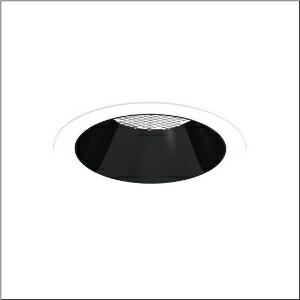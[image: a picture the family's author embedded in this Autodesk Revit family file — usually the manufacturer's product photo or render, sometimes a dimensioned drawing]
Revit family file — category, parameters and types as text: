
# Revit family: lunis_21_xl_51db17ef91c
name_source: partatom
category: Lighting Fixtures
units: mm (PartAtom-declared; Revit-internal decimal feet)

## family parameters
Cut with Voids When Loaded = No
Host = Face
Light Source = No
Part Type = Normal
Room Calculation Point = No
Round Connector Dimension = Use Diameter
Shared = No

## types (1)
- --- (1 x LED, 3480 lm, 25.4 W, 6500K)
    Apparent Load = 25 VA
    CIE Flux Codes = 92 100 100 100 100
    Color Rendering = 80
    Color Temperature = 6500K
    Default Elevation = 1800 mm
    Description = Lunis 21,  XL, downlight, light control with lens, of PMMA, anti glare with reflector, of PC, light emission: direct distribution, LED rated luminous flux: 2.060lm, light colour: 830/840/865, with terminal, 5-pole, mains connection: 220..240V, AC/DC, 0/50..60Hz, housing, round, of diecast aluminium, traffic white (RAL 9016), diameter: 230mm, clamping range: 1..40mm, protection rating (complete): IP20, protection rating (on room side): IP54, insulation class (complete): insulation class II (safety insulation), certification: CE, impact resistance: IK03, packaging unit: 1 piece
    Height = 0 mm  [stored 0 ft]
    Lamp = 1 x LED
    Lamp Light Flux = 3480 lm
    Lamp Power = 25.4 W
    Lamp count = 1
    Length = 230 mm
    Luminous efficacy = 137 lm/W
    Manufacturer = Siteco
    ModVariant = No
    Model = 51DB17EF91C
    Mounting Place = Ceiling
    Mounting Type = Recessed
    Number of Poles = 1
    OnlyDefault = Yes
    Power Factor = 1
    Product Name = Lunis 21 XL
    Product group = downlight
    ProductGroupID = 400
    Protection Class = Protection class II
    Protection Degree = IP 20
    RLX_Detail_Level = 1
    RLX_Emergency_Light_Flux = 0 lm
    RLX_Emergency_Type = 0
    RLX_Emergency_Type_DB = No
    RlxData = <blob elided: 22649 chars, md5=8bca8684>
    Socket = socket
    Standby Power = 0 W
    System Light Flux = 3480 lm
    System Power = 25 W
    Type Comments = individual setting: colour temperature 6500K, luminous flux: 100 % | (ON | ON | OFF | OFF) | 700 mA
    Type Image = l_1291161.jpg
    URL = http://relux.com
    VarID = @adj_019750
    Voltage = 0 V
    Weight = 0.00 kg
    Width = 0 mm  [stored 0 ft]

note: [stored X ft] marks values corroborated as IEEE doubles in the binary element streams (Revit-internal decimal feet)

## geometry (parser evidence)
native form markers: Blend x4, Sweep x11
no freeform markers — native parametric forms only
